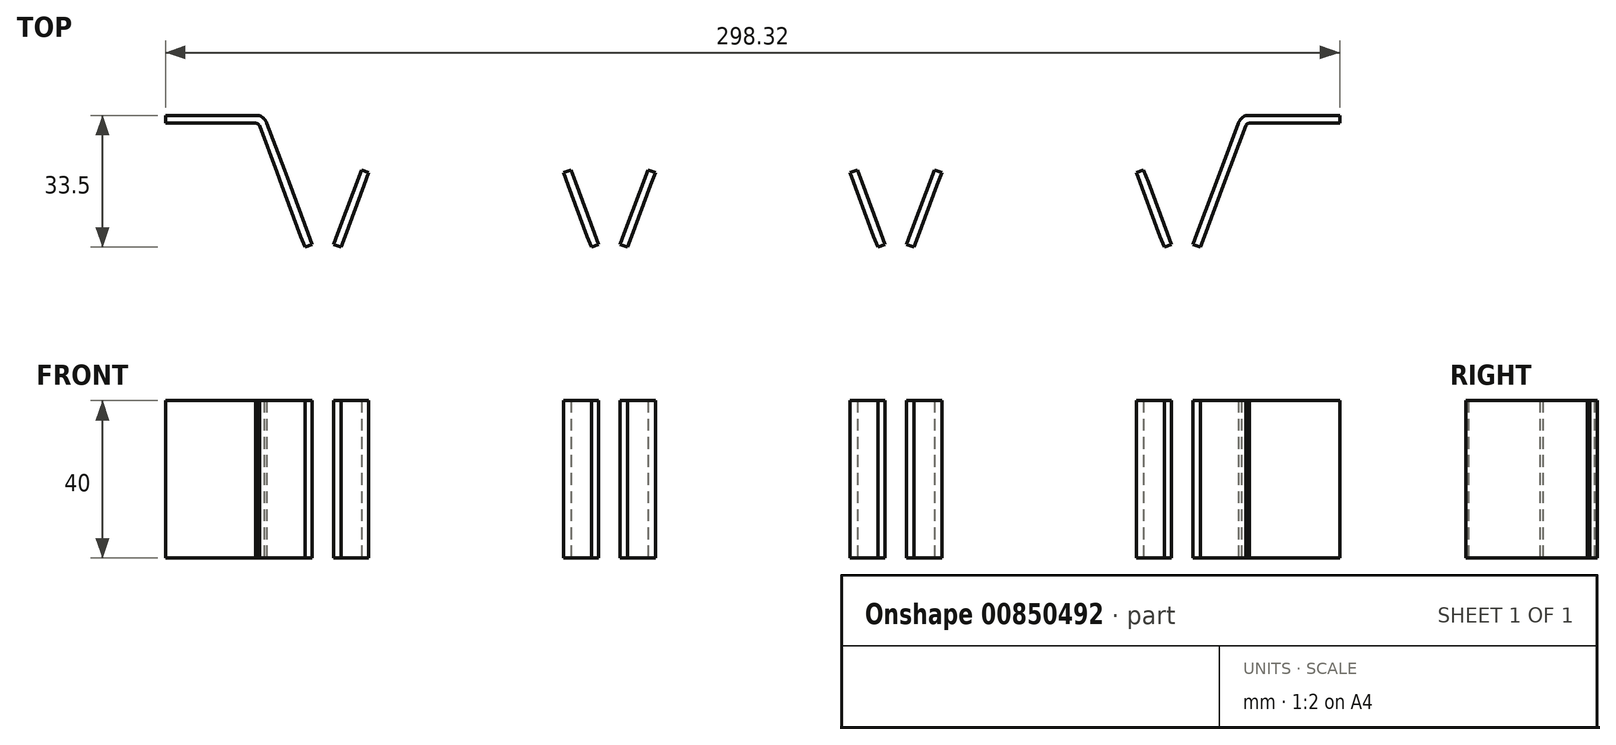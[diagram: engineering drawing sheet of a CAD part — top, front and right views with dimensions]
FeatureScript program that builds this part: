
annotation { "Feature Type Name" : "Feature", "Feature Type Description" : "" }
export const myFeature = defineFeature(function(context is Context, id is Id, definition is map)
    precondition{}
    {
        {
            var Q0;
            Q0=qCreatedBy(makeId("Top.planeOp"),FACE);
            var sketch = newSketch(context, id + "F0", { "sketchPlane" : qUnion([Q0])});
            skLineSegment(sketch, "E0", {"start": v(-19.34, 19) * mm, "end": v(19.34, 19) * mm});
            skLineSegment(sketch, "E1", {"start": v(100.51, 4.06) * mm, "end": v(98.64, 3.36) * mm});
            skLineSegment(sketch, "E2", {"start": v(119.68, 3.36) * mm, "end": v(117.8, 4.06) * mm});
            skLineSegment(sketch, "E3", {"start": v(-117.8, 4.06) * mm, "end": v(-119.68, 3.36) * mm});
            skLineSegment(sketch, "E4", {"start": v(-98.64, 3.36) * mm, "end": v(-100.51, 4.06) * mm});
            skLineSegment(sketch, "E5", {"start": v(27.74, 4.06) * mm, "end": v(25.87, 3.36) * mm});
            skLineSegment(sketch, "E6", {"start": v(46.9, 3.36) * mm, "end": v(45.03, 4.06) * mm});
            skLineSegment(sketch, "E7", {"start": v(-45.03, 4.06) * mm, "end": v(-46.9, 3.36) * mm});
            skLineSegment(sketch, "E8", {"start": v(-25.87, 3.36) * mm, "end": v(-27.74, 4.06) * mm});
            skArc(sketch, "E9", {"start": v(124.14, 20.14) * mm, "mid": v(123.7, 19.61) * mm, "end": v(123.4, 19) * mm});
            skLineSegment(sketch, "E10", {"start": v(125.87, 18.93) * mm, "end": v(126.24, 19) * mm});
            skLineSegment(sketch, "E11", {"start": v(125.52, 18.7) * mm, "end": v(125.6, 18.77) * mm});
            skLineSegment(sketch, "E12", {"start": v(125.34, 18.45) * mm, "end": v(125.38, 18.52) * mm});
            skLineSegment(sketch, "E13", {"start": v(126.24, 19) * mm, "end": v(145.16, 19) * mm});
            skLineSegment(sketch, "E14", {"start": v(92.71, 18.77) * mm, "end": v(92.82, 18.67) * mm});
            skLineSegment(sketch, "E15", {"start": v(92.58, 18.86) * mm, "end": v(92.62, 18.84) * mm});
            skLineSegment(sketch, "E16", {"start": v(92.08, 19) * mm, "end": v(92.45, 18.93) * mm});
            skLineSegment(sketch, "E17", {"start": v(94.88, 19.07) * mm, "end": v(94.85, 19.15) * mm});
            skLineSegment(sketch, "E18", {"start": v(59.7, 21) * mm, "end": v(55.96, 21) * mm});
            skLineSegment(sketch, "E19", {"start": v(92.04, 21) * mm, "end": v(91.03, 21) * mm});
            skLineSegment(sketch, "E20", {"start": v(53.1, 18.93) * mm, "end": v(53.47, 19) * mm});
            skLineSegment(sketch, "E21", {"start": v(52.86, 18.8) * mm, "end": v(52.96, 18.86) * mm});
            skLineSegment(sketch, "E22", {"start": v(52.72, 18.67) * mm, "end": v(52.83, 18.77) * mm});
            skLineSegment(sketch, "E23", {"start": v(50.7, 19.15) * mm, "end": v(50.67, 19.08) * mm});
            skLineSegment(sketch, "E24", {"start": v(50.79, 19.35) * mm, "end": v(50.77, 19.31) * mm});
            skLineSegment(sketch, "E25", {"start": v(19.94, 18.77) * mm, "end": v(20.05, 18.67) * mm});
            skLineSegment(sketch, "E26", {"start": v(19.81, 18.86) * mm, "end": v(19.85, 18.84) * mm});
            skLineSegment(sketch, "E27", {"start": v(19.34, 19) * mm, "end": v(19.68, 18.93) * mm});
            skLineSegment(sketch, "E28", {"start": v(19.27, 21) * mm, "end": v(18.25, 21) * mm});
            skLineSegment(sketch, "E29", {"start": v(-19.68, 18.93) * mm, "end": v(-19.34, 19) * mm});
            skLineSegment(sketch, "E30", {"start": v(-19.9, 18.8) * mm, "end": v(-19.81, 18.86) * mm});
            skLineSegment(sketch, "E31", {"start": v(-20.05, 18.67) * mm, "end": v(-19.94, 18.77) * mm});
            skLineSegment(sketch, "E32", {"start": v(-21.99, 19.35) * mm, "end": v(-22, 19.31) * mm});
            skLineSegment(sketch, "E33", {"start": v(-52.83, 18.77) * mm, "end": v(-52.72, 18.67) * mm});
            skLineSegment(sketch, "E34", {"start": v(-52.96, 18.86) * mm, "end": v(-52.93, 18.84) * mm});
            skLineSegment(sketch, "E35", {"start": v(-53.47, 19) * mm, "end": v(-53.1, 18.93) * mm});
            skLineSegment(sketch, "E36", {"start": v(-50.66, 19.07) * mm, "end": v(-50.7, 19.15) * mm});
            skLineSegment(sketch, "E37", {"start": v(-85.85, 21) * mm, "end": v(-89.58, 21) * mm});
            skLineSegment(sketch, "E38", {"start": v(-53.5, 21) * mm, "end": v(-54.52, 21) * mm});
            skLineSegment(sketch, "E39", {"start": v(-92.45, 18.93) * mm, "end": v(-92.08, 19) * mm});
            skLineSegment(sketch, "E40", {"start": v(-92.68, 18.8) * mm, "end": v(-92.58, 18.86) * mm});
            skLineSegment(sketch, "E41", {"start": v(-92.82, 18.67) * mm, "end": v(-92.71, 18.77) * mm});
            skLineSegment(sketch, "E42", {"start": v(-94.85, 19.15) * mm, "end": v(-94.88, 19.08) * mm});
            skLineSegment(sketch, "E43", {"start": v(-94.76, 19.35) * mm, "end": v(-94.78, 19.31) * mm});
            skArc(sketch, "E44", {"start": v(-123.4, 19) * mm, "mid": v(-123.7, 19.61) * mm, "end": v(-124.14, 20.14) * mm});
            skLineSegment(sketch, "E45", {"start": v(-125.87, 18.93) * mm, "end": v(-126.24, 19) * mm});
            skLineSegment(sketch, "E46", {"start": v(-125.52, 18.7) * mm, "end": v(-125.6, 18.77) * mm});
            skLineSegment(sketch, "E47", {"start": v(-125.34, 18.45) * mm, "end": v(-125.38, 18.52) * mm});
            skLineSegment(sketch, "E48", {"start": v(-126.24, 19) * mm, "end": v(-145.16, 19) * mm});
            skLineSegment(sketch, "E49", {"start": v(125.6, 18.77) * mm, "end": v(125.87, 18.93) * mm});
            skLineSegment(sketch, "E50", {"start": v(125.38, 18.52) * mm, "end": v(125.52, 18.7) * mm});
            skLineSegment(sketch, "E51", {"start": v(125.3, 18.35) * mm, "end": v(125.34, 18.45) * mm});
            skLineSegment(sketch, "E52", {"start": v(120.82, 6.41) * mm, "end": v(125.3, 18.35) * mm});
            skLineSegment(sketch, "E53", {"start": v(93.02, 18.35) * mm, "end": v(97.5, 6.41) * mm});
            skLineSegment(sketch, "E54", {"start": v(92.82, 18.67) * mm, "end": v(93.02, 18.35) * mm});
            skLineSegment(sketch, "E55", {"start": v(92.62, 18.84) * mm, "end": v(92.71, 18.77) * mm});
            skLineSegment(sketch, "E56", {"start": v(92.45, 18.93) * mm, "end": v(92.58, 18.86) * mm});
            skLineSegment(sketch, "E57", {"start": v(92.08, 19) * mm, "end": v(53.47, 19) * mm});
            skLineSegment(sketch, "E58", {"start": v(94.89, 19.05) * mm, "end": v(94.9, 19) * mm});
            skLineSegment(sketch, "E59", {"start": v(50.64, 19) * mm, "end": v(50.66, 19.05) * mm});
            skLineSegment(sketch, "E60", {"start": v(52.96, 18.86) * mm, "end": v(53.1, 18.93) * mm});
            skLineSegment(sketch, "E61", {"start": v(52.83, 18.77) * mm, "end": v(52.86, 18.8) * mm});
            skLineSegment(sketch, "E62", {"start": v(52.53, 18.35) * mm, "end": v(52.72, 18.67) * mm});
            skLineSegment(sketch, "E63", {"start": v(48.05, 6.41) * mm, "end": v(52.53, 18.35) * mm});
            skLineSegment(sketch, "E64", {"start": v(20.24, 18.35) * mm, "end": v(24.72, 6.41) * mm});
            skLineSegment(sketch, "E65", {"start": v(145.16, 21) * mm, "end": v(149.16, 21) * mm});
            skLineSegment(sketch, "E66", {"start": v(145.16, 21) * mm, "end": v(145.16, 19) * mm});
            skLineSegment(sketch, "E67", {"start": v(149.16, 19) * mm, "end": v(145.16, 19) * mm});
            skLineSegment(sketch, "E68", {"start": v(149.16, 21) * mm, "end": v(149.16, 19) * mm});
            skLineSegment(sketch, "E69", {"start": v(103.54, -9.73) * mm, "end": v(104.58, -12.5) * mm});
            skLineSegment(sketch, "E70", {"start": v(113.73, -12.5) * mm, "end": v(114.77, -9.73) * mm});
            skLineSegment(sketch, "E71", {"start": v(106.46, -11.8) * mm, "end": v(104.58, -12.5) * mm});
            skLineSegment(sketch, "E72", {"start": v(111.86, -11.8) * mm, "end": v(113.73, -12.5) * mm});
            skLineSegment(sketch, "E73", {"start": v(97.5, 6.41) * mm, "end": v(98.64, 3.36) * mm});
            skLineSegment(sketch, "E74", {"start": v(97.5, 6.41) * mm, "end": v(99.37, 7.11) * mm});
            skLineSegment(sketch, "E75", {"start": v(119.68, 3.36) * mm, "end": v(120.82, 6.41) * mm});
            skLineSegment(sketch, "E76", {"start": v(120.82, 6.41) * mm, "end": v(118.95, 7.11) * mm});
            skLineSegment(sketch, "E77", {"start": v(112.9, -9.03) * mm, "end": v(111.86, -11.8) * mm});
            skLineSegment(sketch, "E78", {"start": v(118.95, 7.11) * mm, "end": v(117.8, 4.06) * mm});
            skLineSegment(sketch, "E79", {"start": v(123.4, 19) * mm, "end": v(118.95, 7.11) * mm});
            skLineSegment(sketch, "E80", {"start": v(111.86, -11.8) * mm, "end": v(109.16, -19) * mm});
            skLineSegment(sketch, "E81", {"start": v(106.46, -11.8) * mm, "end": v(105.42, -9.03) * mm});
            skLineSegment(sketch, "E82", {"start": v(109.16, -19) * mm, "end": v(106.46, -11.8) * mm});
            skLineSegment(sketch, "E83", {"start": v(99.37, 7.11) * mm, "end": v(94.9, 19) * mm});
            skLineSegment(sketch, "E84", {"start": v(100.51, 4.06) * mm, "end": v(99.37, 7.11) * mm});
            skLineSegment(sketch, "E85", {"start": v(105.42, -9.03) * mm, "end": v(100.51, 4.06) * mm});
            skLineSegment(sketch, "E86", {"start": v(98.64, 3.36) * mm, "end": v(103.54, -9.73) * mm});
            skLineSegment(sketch, "E87", {"start": v(105.42, -9.03) * mm, "end": v(103.54, -9.73) * mm});
            skLineSegment(sketch, "E88", {"start": v(112.9, -9.03) * mm, "end": v(117.8, 4.06) * mm});
            skLineSegment(sketch, "E89", {"start": v(119.68, 3.36) * mm, "end": v(114.77, -9.73) * mm});
            skLineSegment(sketch, "E90", {"start": v(112.9, -9.03) * mm, "end": v(114.77, -9.73) * mm});
            skLineSegment(sketch, "E91", {"start": v(-125.34, 18.45) * mm, "end": v(-125.3, 18.35) * mm});
            skLineSegment(sketch, "E92", {"start": v(-125.52, 18.7) * mm, "end": v(-125.38, 18.52) * mm});
            skLineSegment(sketch, "E93", {"start": v(-125.87, 18.93) * mm, "end": v(-125.6, 18.77) * mm});
            skLineSegment(sketch, "E94", {"start": v(-97.5, 6.41) * mm, "end": v(-93.02, 18.35) * mm});
            skLineSegment(sketch, "E95", {"start": v(-125.3, 18.35) * mm, "end": v(-120.82, 6.41) * mm});
            skLineSegment(sketch, "E96", {"start": v(-52.96, 18.86) * mm, "end": v(-53.1, 18.93) * mm});
            skLineSegment(sketch, "E97", {"start": v(-52.83, 18.77) * mm, "end": v(-52.93, 18.84) * mm});
            skLineSegment(sketch, "E98", {"start": v(-52.53, 18.35) * mm, "end": v(-52.72, 18.67) * mm});
            skLineSegment(sketch, "E99", {"start": v(-50.66, 19.05) * mm, "end": v(-50.64, 19) * mm});
            skLineSegment(sketch, "E100", {"start": v(-94.9, 19) * mm, "end": v(-94.89, 19.05) * mm});
            skLineSegment(sketch, "E101", {"start": v(-53.47, 19) * mm, "end": v(-92.08, 19) * mm});
            skLineSegment(sketch, "E102", {"start": v(-24.72, 6.41) * mm, "end": v(-20.24, 18.35) * mm});
            skLineSegment(sketch, "E103", {"start": v(-52.53, 18.35) * mm, "end": v(-48.05, 6.41) * mm});
            skLineSegment(sketch, "E104", {"start": v(-92.58, 18.86) * mm, "end": v(-92.45, 18.93) * mm});
            skLineSegment(sketch, "E105", {"start": v(-92.71, 18.77) * mm, "end": v(-92.68, 18.8) * mm});
            skLineSegment(sketch, "E106", {"start": v(-93.02, 18.35) * mm, "end": v(-92.82, 18.67) * mm});
            skLineSegment(sketch, "E107", {"start": v(-145.16, 19) * mm, "end": v(-149.16, 19) * mm});
            skLineSegment(sketch, "E108", {"start": v(-145.16, 19) * mm, "end": v(-145.16, 21) * mm});
            skLineSegment(sketch, "E109", {"start": v(-149.16, 21) * mm, "end": v(-145.16, 21) * mm});
            skLineSegment(sketch, "E110", {"start": v(-149.16, 19) * mm, "end": v(-149.16, 21) * mm});
            skLineSegment(sketch, "E111", {"start": v(-114.77, -9.73) * mm, "end": v(-113.73, -12.5) * mm});
            skLineSegment(sketch, "E112", {"start": v(-104.58, -12.5) * mm, "end": v(-103.54, -9.73) * mm});
            skLineSegment(sketch, "E113", {"start": v(-111.86, -11.8) * mm, "end": v(-113.73, -12.5) * mm});
            skLineSegment(sketch, "E114", {"start": v(-106.46, -11.8) * mm, "end": v(-104.58, -12.5) * mm});
            skLineSegment(sketch, "E115", {"start": v(-120.82, 6.41) * mm, "end": v(-119.68, 3.36) * mm});
            skLineSegment(sketch, "E116", {"start": v(-120.82, 6.41) * mm, "end": v(-118.95, 7.11) * mm});
            skLineSegment(sketch, "E117", {"start": v(-98.64, 3.36) * mm, "end": v(-97.5, 6.41) * mm});
            skLineSegment(sketch, "E118", {"start": v(-97.5, 6.41) * mm, "end": v(-99.37, 7.11) * mm});
            skLineSegment(sketch, "E119", {"start": v(-105.42, -9.03) * mm, "end": v(-106.46, -11.8) * mm});
            skLineSegment(sketch, "E120", {"start": v(-99.37, 7.11) * mm, "end": v(-100.51, 4.06) * mm});
            skLineSegment(sketch, "E121", {"start": v(-94.9, 19) * mm, "end": v(-99.37, 7.11) * mm});
            skLineSegment(sketch, "E122", {"start": v(-106.46, -11.8) * mm, "end": v(-109.16, -19) * mm});
            skLineSegment(sketch, "E123", {"start": v(-111.86, -11.8) * mm, "end": v(-112.9, -9.03) * mm});
            skLineSegment(sketch, "E124", {"start": v(-109.16, -19) * mm, "end": v(-111.86, -11.8) * mm});
            skLineSegment(sketch, "E125", {"start": v(-118.95, 7.11) * mm, "end": v(-123.4, 19) * mm});
            skLineSegment(sketch, "E126", {"start": v(-117.8, 4.06) * mm, "end": v(-118.95, 7.11) * mm});
            skLineSegment(sketch, "E127", {"start": v(-112.9, -9.03) * mm, "end": v(-117.8, 4.06) * mm});
            skLineSegment(sketch, "E128", {"start": v(-119.68, 3.36) * mm, "end": v(-114.77, -9.73) * mm});
            skLineSegment(sketch, "E129", {"start": v(-112.9, -9.03) * mm, "end": v(-114.77, -9.73) * mm});
            skLineSegment(sketch, "E130", {"start": v(-105.42, -9.03) * mm, "end": v(-100.51, 4.06) * mm});
            skLineSegment(sketch, "E131", {"start": v(-98.64, 3.36) * mm, "end": v(-103.54, -9.73) * mm});
            skLineSegment(sketch, "E132", {"start": v(-105.42, -9.03) * mm, "end": v(-103.54, -9.73) * mm});
            skLineSegment(sketch, "E133", {"start": v(20.05, 18.67) * mm, "end": v(20.24, 18.35) * mm});
            skLineSegment(sketch, "E134", {"start": v(19.85, 18.84) * mm, "end": v(19.94, 18.77) * mm});
            skLineSegment(sketch, "E135", {"start": v(19.68, 18.93) * mm, "end": v(19.81, 18.86) * mm});
            skLineSegment(sketch, "E136", {"start": v(30.77, -9.73) * mm, "end": v(31.81, -12.5) * mm});
            skLineSegment(sketch, "E137", {"start": v(40.96, -12.5) * mm, "end": v(42, -9.73) * mm});
            skLineSegment(sketch, "E138", {"start": v(33.69, -11.8) * mm, "end": v(31.81, -12.5) * mm});
            skLineSegment(sketch, "E139", {"start": v(39.09, -11.8) * mm, "end": v(40.96, -12.5) * mm});
            skLineSegment(sketch, "E140", {"start": v(24.72, 6.41) * mm, "end": v(25.87, 3.36) * mm});
            skLineSegment(sketch, "E141", {"start": v(24.72, 6.41) * mm, "end": v(26.6, 7.11) * mm});
            skLineSegment(sketch, "E142", {"start": v(46.9, 3.36) * mm, "end": v(48.05, 6.41) * mm});
            skLineSegment(sketch, "E143", {"start": v(48.05, 6.41) * mm, "end": v(46.18, 7.11) * mm});
            skLineSegment(sketch, "E144", {"start": v(40.13, -9.03) * mm, "end": v(39.09, -11.8) * mm});
            skLineSegment(sketch, "E145", {"start": v(46.18, 7.11) * mm, "end": v(45.03, 4.06) * mm});
            skLineSegment(sketch, "E146", {"start": v(50.64, 19) * mm, "end": v(46.18, 7.11) * mm});
            skLineSegment(sketch, "E147", {"start": v(39.09, -11.8) * mm, "end": v(36.39, -19) * mm});
            skLineSegment(sketch, "E148", {"start": v(33.69, -11.8) * mm, "end": v(32.65, -9.03) * mm});
            skLineSegment(sketch, "E149", {"start": v(36.39, -19) * mm, "end": v(33.69, -11.8) * mm});
            skLineSegment(sketch, "E150", {"start": v(26.6, 7.11) * mm, "end": v(22.14, 19) * mm});
            skLineSegment(sketch, "E151", {"start": v(27.74, 4.06) * mm, "end": v(26.6, 7.11) * mm});
            skLineSegment(sketch, "E152", {"start": v(32.65, -9.03) * mm, "end": v(27.74, 4.06) * mm});
            skLineSegment(sketch, "E153", {"start": v(25.87, 3.36) * mm, "end": v(30.77, -9.73) * mm});
            skLineSegment(sketch, "E154", {"start": v(32.65, -9.03) * mm, "end": v(30.77, -9.73) * mm});
            skLineSegment(sketch, "E155", {"start": v(40.13, -9.03) * mm, "end": v(45.03, 4.06) * mm});
            skLineSegment(sketch, "E156", {"start": v(46.9, 3.36) * mm, "end": v(42, -9.73) * mm});
            skLineSegment(sketch, "E157", {"start": v(40.13, -9.03) * mm, "end": v(42, -9.73) * mm});
            skLineSegment(sketch, "E158", {"start": v(-19.81, 18.86) * mm, "end": v(-19.68, 18.93) * mm});
            skLineSegment(sketch, "E159", {"start": v(-19.94, 18.77) * mm, "end": v(-19.9, 18.8) * mm});
            skLineSegment(sketch, "E160", {"start": v(-20.24, 18.35) * mm, "end": v(-20.05, 18.67) * mm});
            skLineSegment(sketch, "E161", {"start": v(-42, -9.73) * mm, "end": v(-40.96, -12.5) * mm});
            skLineSegment(sketch, "E162", {"start": v(-31.81, -12.5) * mm, "end": v(-30.77, -9.73) * mm});
            skLineSegment(sketch, "E163", {"start": v(-39.09, -11.8) * mm, "end": v(-40.96, -12.5) * mm});
            skLineSegment(sketch, "E164", {"start": v(-33.69, -11.8) * mm, "end": v(-31.81, -12.5) * mm});
            skLineSegment(sketch, "E165", {"start": v(-48.05, 6.41) * mm, "end": v(-46.9, 3.36) * mm});
            skLineSegment(sketch, "E166", {"start": v(-48.05, 6.41) * mm, "end": v(-46.18, 7.11) * mm});
            skLineSegment(sketch, "E167", {"start": v(-25.87, 3.36) * mm, "end": v(-24.72, 6.41) * mm});
            skLineSegment(sketch, "E168", {"start": v(-24.72, 6.41) * mm, "end": v(-26.6, 7.11) * mm});
            skLineSegment(sketch, "E169", {"start": v(-32.65, -9.03) * mm, "end": v(-33.69, -11.8) * mm});
            skLineSegment(sketch, "E170", {"start": v(-26.6, 7.11) * mm, "end": v(-27.74, 4.06) * mm});
            skLineSegment(sketch, "E171", {"start": v(-22.14, 19) * mm, "end": v(-26.6, 7.11) * mm});
            skLineSegment(sketch, "E172", {"start": v(-33.69, -11.8) * mm, "end": v(-36.39, -19) * mm});
            skLineSegment(sketch, "E173", {"start": v(-39.09, -11.8) * mm, "end": v(-40.13, -9.03) * mm});
            skLineSegment(sketch, "E174", {"start": v(-36.39, -19) * mm, "end": v(-39.09, -11.8) * mm});
            skLineSegment(sketch, "E175", {"start": v(-46.18, 7.11) * mm, "end": v(-50.64, 19) * mm});
            skLineSegment(sketch, "E176", {"start": v(-45.03, 4.06) * mm, "end": v(-46.18, 7.11) * mm});
            skLineSegment(sketch, "E177", {"start": v(-40.13, -9.03) * mm, "end": v(-45.03, 4.06) * mm});
            skLineSegment(sketch, "E178", {"start": v(-46.9, 3.36) * mm, "end": v(-42, -9.73) * mm});
            skLineSegment(sketch, "E179", {"start": v(-40.13, -9.03) * mm, "end": v(-42, -9.73) * mm});
            skLineSegment(sketch, "E180", {"start": v(-32.65, -9.03) * mm, "end": v(-27.74, 4.06) * mm});
            skLineSegment(sketch, "E181", {"start": v(-25.87, 3.36) * mm, "end": v(-30.77, -9.73) * mm});
            skLineSegment(sketch, "E182", {"start": v(-32.65, -9.03) * mm, "end": v(-30.77, -9.73) * mm});
            skLineSegment(sketch, "E183", {"start": v(-54.75, 21) * mm, "end": v(-53.47, 21) * mm});
            skLineSegment(sketch, "E184", {"start": v(-92.08, 21) * mm, "end": v(-90.8, 21) * mm});
            skLineSegment(sketch, "E185", {"start": v(-94.6, 19.64) * mm, "end": v(-94.35, 19.96) * mm});
            skLineSegment(sketch, "E186", {"start": v(18.02, 21) * mm, "end": v(19.3, 21) * mm});
            skLineSegment(sketch, "E187", {"start": v(-19.3, 21) * mm, "end": v(-18.03, 21) * mm});
            skLineSegment(sketch, "E188", {"start": v(-21.82, 19.64) * mm, "end": v(-21.58, 19.96) * mm});
            skLineSegment(sketch, "E189", {"start": v(90.8, 21) * mm, "end": v(92.08, 21) * mm});
            skLineSegment(sketch, "E190", {"start": v(53.47, 21) * mm, "end": v(54.74, 21) * mm});
            skLineSegment(sketch, "E191", {"start": v(50.95, 19.64) * mm, "end": v(51.2, 19.96) * mm});
            skLineSegment(sketch, "E192", {"start": v(-22.12, 19.05) * mm, "end": v(-22.14, 19) * mm});
            skLineSegment(sketch, "E193", {"start": v(22.14, 19) * mm, "end": v(22.12, 19.05) * mm});
            skFitSpline(sketch, "E194", {"points": [v(145.16, 21) * mm, v(138.85, 21) * mm, v(132.52, 21) * mm, v(126.18, 21) * mm, v(125.78, 20.99) * mm, v(125.03, 20.82) * mm, v(124.4, 20.4) * mm, v(124.14, 20.14) * mm]});
            skFitSpline(sketch, "E195", {"points": [v(-145.16, 21) * mm, v(-138.85, 21) * mm, v(-132.52, 21) * mm, v(-126.18, 21) * mm, v(-125.78, 20.99) * mm, v(-125.03, 20.82) * mm, v(-124.4, 20.4) * mm, v(-124.14, 20.14) * mm]});
            skFitSpline(sketch, "E196", {"points": [v(50.66, 19.05) * mm, v(1000, 51.39) * mm, v(21, 821.93) * mm, v(53.47, 21) * mm, v(1000, 72.77) * mm, v(21, 1000) * mm, v(92.08, 21) * mm]});
            skFitSpline(sketch, "E197", {"points": [v(104.58, -12.5) * mm, v(1000, 105.48) * mm, v(-14.9, 1000) * mm, v(106.38, -17.3) * mm, v(1000, 107.29) * mm, v(-19.7, 1000) * mm, v(107.59, -20.5) * mm, v(881.28, 108.3) * mm, v(-21, 881.28) * mm, v(109.16, -21) * mm, v(1000, 110.02) * mm, v(-21, 881.28) * mm, v(110.73, -20.5) * mm]});
            skFitSpline(sketch, "E198", {"points": [v(-94.89, 19.05) * mm, v(1000, -94.16) * mm, v(21, 821.93) * mm, v(-92.08, 21) * mm, v(1000, -72.77) * mm, v(21, 1000) * mm, v(-53.47, 21) * mm]});
            skFitSpline(sketch, "E199", {"points": [v(-113.73, -12.5) * mm, v(1000, -112.83) * mm, v(-14.9, 1000) * mm, v(-111.93, -17.3) * mm, v(1000, -111.03) * mm, v(-19.7, 1000) * mm, v(-110.73, -20.5) * mm, v(881.28, -110.02) * mm, v(-21, 881.28) * mm, v(-109.16, -21) * mm, v(1000, -108.3) * mm, v(-21, 881.28) * mm, v(-107.59, -20.5) * mm]});
            skFitSpline(sketch, "E200", {"points": [v(31.81, -12.5) * mm, v(1000, 32.71) * mm, v(-14.9, 1000) * mm, v(33.61, -17.3) * mm, v(1000, 34.51) * mm, v(-19.7, 1000) * mm, v(34.82, -20.5) * mm, v(881.28, 35.52) * mm, v(-21, 881.28) * mm, v(36.39, -21) * mm, v(1000, 37.25) * mm, v(-21, 881.28) * mm, v(37.96, -20.5) * mm]});
            skFitSpline(sketch, "E201", {"points": [v(-40.96, -12.5) * mm, v(1000, -40.06) * mm, v(-14.9, 1000) * mm, v(-39.16, -17.3) * mm, v(1000, -38.26) * mm, v(-19.7, 1000) * mm, v(-37.96, -20.5) * mm, v(881.28, -37.25) * mm, v(-21, 881.28) * mm, v(-36.39, -21) * mm, v(1000, -35.52) * mm, v(-21, 881.28) * mm, v(-34.82, -20.5) * mm]});
            skFitSpline(sketch, "E202", {"points": [v(22.12, 19.05) * mm, v(1000, 21.39) * mm, v(21, 821.93) * mm, v(19.3, 21) * mm, v(1000, 0) * mm, v(21, 1000) * mm, v(-19.3, 21) * mm]});
            skSolve(sketch);
        }
        {
            var Q0;
            Q0 = qSketchRegion(id + "F0", true);
            extrude(context, id + "F1", {"entities" : qUnion([Q0]), "depth" : 40 * mm, "offsetDistance" : 25 * mm});
        }
    });
